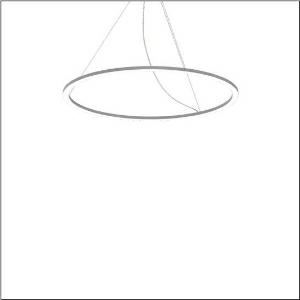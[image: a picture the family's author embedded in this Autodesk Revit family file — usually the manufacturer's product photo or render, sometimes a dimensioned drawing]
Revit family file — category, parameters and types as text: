
# Revit family: silica_21_ring-d_5pjbd3d1204a
name_source: partatom
category: Lighting Fixtures
units: mm (PartAtom-declared; Revit-internal decimal feet)

## family parameters
Cut with Voids When Loaded = No
Host = Face
Light Source = No
Part Type = Normal
Room Calculation Point = No
Round Connector Dimension = Use Diameter
Shared = No

## types (1)
- Silica 21 Ring-D (1 x LED, 8050 lm, 94 W, 3000K)
    Apparent Load = 94 VA
    CIE Flux Codes = 37 69 92 100 100
    Color Rendering = 80
    Color Temperature = 3000K
    Default Elevation = 1800 mm
    Description = Silica 21 Ring-D, suspended luminaire, of PMMA, frosted, light emission: ring underside luminous distribution, primary light characteristic: symmetric, installation type: suspended mounting, LED, rated luminous flux: 8.050lm, luminous efficacy: 86lm/W, light colour: 830, colour temperature: 3000K, control gear: DALI 2, with terminal, 5-pole, mains connection: 230V, AC/DC, 0/50..60Hz, rated input power: 94W, housing, of extruded aluminium section, metallic grey (RAL 9006), diameter: 1.100mm, ceiling canopy, metallic grey (RAL 9006), protection rating (lamp compartment): IP40, insulation class (complete): insulation class I (protective earthing), certification: CE, impact resistance: IK02, permissible operating ambient temperature: 0..+35°C, packaging unit: 1 piece
    Height = 25 mm  [stored 0.082021 ft]
    Lamp = 1 x LED
    Lamp Light Flux = 8050 lm
    Lamp Power = 94 W
    Lamp count = 1
    Length = 1100 mm
    Luminous efficacy = 86 lm/W
    Manufacturer = Siteco
    ModVariant = No
    Model = 5PJBD3D1204A
    Mounting Place = Ceiling
    Mounting Type = Pendant
    Number of Poles = 1
    OnlyDefault = Yes
    Power Factor = 1
    Product Name = Silica 21 Ring-D
    Product group = suspended luminaire
    ProductGroupID = 904
    Protection Class = Protection class I
    Protection Degree = IP 40
    RLX_Detail_Level = 1
    RLX_Emergency_Light_Flux = 0 lm
    RLX_Emergency_Type = 0
    RLX_Emergency_Type_DB = No
    RlxData = <blob elided: 14565 chars, md5=b541848e>
    Socket = socket
    Standby Power = 0 W
    System Light Flux = 8050 lm
    System Power = 94 W
    Type Comments = Product without accessories
    Type Image = l_1251746.jpg
    URL = http://relux.com
    VarID = ---
    Voltage = 0 V
    Weight = 0.00 kg
    Width = 0 mm  [stored 0 ft]

note: [stored X ft] marks values corroborated as IEEE doubles in the binary element streams (Revit-internal decimal feet)

## geometry (parser evidence)
native form markers: Sweep x13
no freeform markers — native parametric forms only
